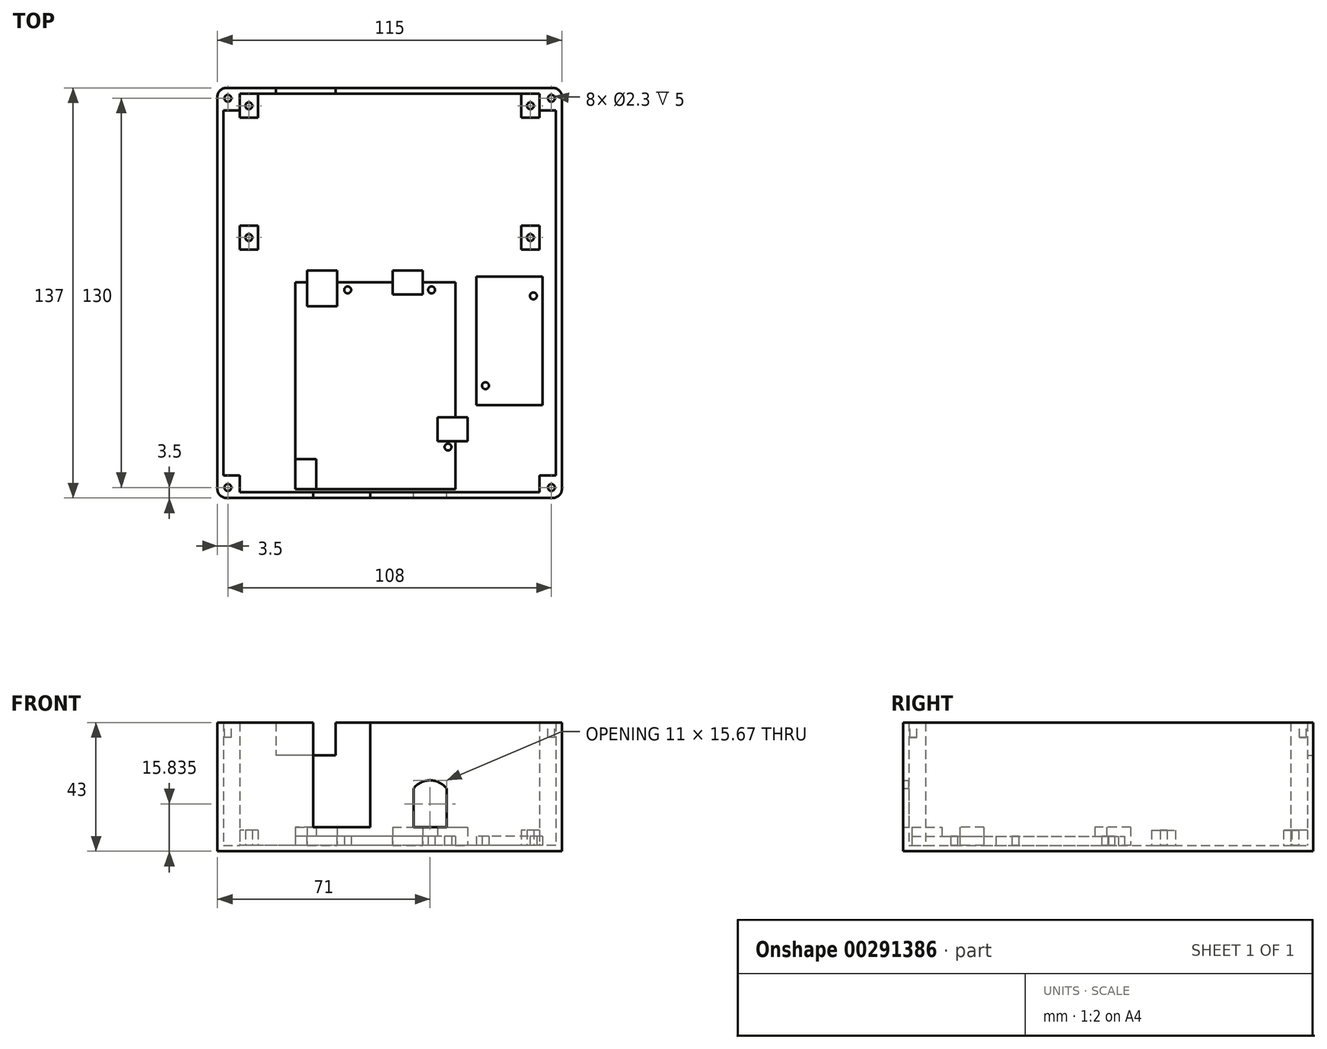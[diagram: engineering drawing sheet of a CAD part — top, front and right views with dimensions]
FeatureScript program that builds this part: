
annotation { "Feature Type Name" : "Feature", "Feature Type Description" : "" }
export const myFeature = defineFeature(function(context is Context, id is Id, definition is map)
    precondition{}
    {
        {
            var Q0;
            Q0=qCreatedBy(makeId("Top.planeOp"),FACE);
            var sketch = newSketch(context, id + "F0", { "sketchPlane" : qUnion([Q0])});
            skLineSegment(sketch, "E0.bottom", {"start": v(57.5, -68.5) * mm, "end": v(-57.5, -68.5) * mm});
            skLineSegment(sketch, "E0.top", {"start": v(57.5, 68.5) * mm, "end": v(-57.5, 68.5) * mm});
            skLineSegment(sketch, "E0.left", {"start": v(57.5, -68.5) * mm, "end": v(57.5, 68.5) * mm});
            skLineSegment(sketch, "E0.right", {"start": v(-57.5, -68.5) * mm, "end": v(-57.5, 68.5) * mm});
            skPoint(sketch, "E0.middle", {"position": v(0, 0) * mm});
            skSolve(sketch);
        }
        {
            var Q0;
            Q0 = qSketchRegion(id + "F0", true);
            extrude(context, id + "F1", {"entities" : qUnion([Q0]), "depth" : 2 * mm});
        }
        {
            var Q0;
            Q0=makeQuery(id+"F1.opExtrude","CAP_FACE",FACE,{"disambiguationData":[OSD([sQuery(id+"F0.wireOp",EDGE,"E0.bottom"),sQuery(id+"F0.wireOp",EDGE,"E0.top"),sQuery(id+"F0.wireOp",EDGE,"E0.left"),sQuery(id+"F0.wireOp",EDGE,"E0.right")])],"isStart":false});
            var sketch = newSketch(context, id + "F2", { "sketchPlane" : qUnion([Q0])});
            skLineSegment(sketch, "E1.bottom", {"start": v(57.5, -68.5) * mm, "end": v(-57.5, -68.5) * mm});
            skLineSegment(sketch, "E1.top", {"start": v(57.5, 68.5) * mm, "end": v(-57.5, 68.5) * mm});
            skLineSegment(sketch, "E1.left", {"start": v(57.5, -68.5) * mm, "end": v(57.5, 68.5) * mm});
            skLineSegment(sketch, "E1.right", {"start": v(-57.5, -68.5) * mm, "end": v(-57.5, 68.5) * mm});
            skPoint(sketch, "E1.middle", {"position": v(0, 0) * mm});
            skLineSegment(sketch, "E2.bottom", {"start": v(55.5, -66.5) * mm, "end": v(-55.5, -66.5) * mm});
            skLineSegment(sketch, "E2.top", {"start": v(55.5, 66.5) * mm, "end": v(-55.5, 66.5) * mm});
            skLineSegment(sketch, "E2.left", {"start": v(55.5, -66.5) * mm, "end": v(55.5, 66.5) * mm});
            skLineSegment(sketch, "E2.right", {"start": v(-55.5, -66.5) * mm, "end": v(-55.5, 66.5) * mm});
            skSolve(sketch);
        }
        {
            var Q0;
            Q0 = qSketchRegion(id + "F2", true);
            extrude(context, id + "F3", {"entities" : qUnion([Q0]), "operationType" : NewBodyOperationType.ADD, "depth" : 41 * mm});
        }
        {
            var Q0;
            Q0=makeQuery(id+"F1.opExtrude","CAP_FACE",FACE,{"disambiguationData":[OSD([sQuery(id+"F0.wireOp",EDGE,"E0.bottom"),sQuery(id+"F0.wireOp",EDGE,"E0.top"),sQuery(id+"F0.wireOp",EDGE,"E0.left"),sQuery(id+"F0.wireOp",EDGE,"E0.right")])],"isStart":false});
            var sketch = newSketch(context, id + "F4", { "sketchPlane" : qUnion([Q0])});
            skLineSegment(sketch, "E3.bottom", {"start": v(50, 15.5) * mm, "end": v(-50, 15.5) * mm, "construction": true});
            skLineSegment(sketch, "E3.top", {"start": v(50, 65.5) * mm, "end": v(-50, 65.5) * mm, "construction": true});
            skLineSegment(sketch, "E3.left", {"start": v(50, 15.5) * mm, "end": v(50, 65.5) * mm, "construction": true});
            skLineSegment(sketch, "E3.right", {"start": v(-50, 15.5) * mm, "end": v(-50, 65.5) * mm, "construction": true});
            skPoint(sketch, "E3.middle", {"position": v(0, 40.5) * mm});
            skCircle(sketch, "E4", {"center": v(-47, 62.5) * mm, "radius": 1.15 * mm});
            skCircle(sketch, "E5", {"center": v(47, 62.5) * mm, "radius": 1.15 * mm});
            skCircle(sketch, "E6", {"center": v(-47, 18.5) * mm, "radius": 1.15 * mm});
            skCircle(sketch, "E7", {"center": v(47, 18.5) * mm, "radius": 1.15 * mm});
            skLineSegment(sketch, "E8.bottom", {"start": v(-44, 66.5) * mm, "end": v(-50, 66.5) * mm});
            skLineSegment(sketch, "E8.top", {"start": v(-44, 58.5) * mm, "end": v(-50, 58.5) * mm});
            skLineSegment(sketch, "E8.left", {"start": v(-44, 66.5) * mm, "end": v(-44, 58.5) * mm});
            skLineSegment(sketch, "E8.right", {"start": v(-50, 66.5) * mm, "end": v(-50, 58.5) * mm});
            skLineSegment(sketch, "E9.bottom", {"start": v(50, 58.5) * mm, "end": v(44, 58.5) * mm});
            skLineSegment(sketch, "E9.top", {"start": v(50, 66.5) * mm, "end": v(44, 66.5) * mm});
            skLineSegment(sketch, "E9.left", {"start": v(50, 58.5) * mm, "end": v(50, 66.5) * mm});
            skLineSegment(sketch, "E9.right", {"start": v(44, 58.5) * mm, "end": v(44, 66.5) * mm});
            skLineSegment(sketch, "E10.bottom", {"start": v(-44, 14.5) * mm, "end": v(-50, 14.5) * mm});
            skLineSegment(sketch, "E10.top", {"start": v(-44, 22.5) * mm, "end": v(-50, 22.5) * mm});
            skLineSegment(sketch, "E10.left", {"start": v(-44, 14.5) * mm, "end": v(-44, 22.5) * mm});
            skLineSegment(sketch, "E10.right", {"start": v(-50, 14.5) * mm, "end": v(-50, 22.5) * mm});
            skLineSegment(sketch, "E11.bottom", {"start": v(50, 14.5) * mm, "end": v(44, 14.5) * mm});
            skLineSegment(sketch, "E11.top", {"start": v(50, 22.5) * mm, "end": v(44, 22.5) * mm});
            skLineSegment(sketch, "E11.left", {"start": v(50, 14.5) * mm, "end": v(50, 22.5) * mm});
            skLineSegment(sketch, "E11.right", {"start": v(44, 14.5) * mm, "end": v(44, 22.5) * mm});
            skSolve(sketch);
        }
        {
            var Q0;
            Q0 = qSketchRegion(id + "F4", true);
            extrude(context, id + "F5", {"entities" : qUnion([Q0]), "operationType" : NewBodyOperationType.ADD, "depth" : 5 * mm});
        }
        {
            var Q0;
            Q0=makeQuery(id+"F5.boolean.opBoolean","SPLIT",FACE,{"disambiguationData":[TD([makeQuery(id+"F3.opExtrude","SWEPT_FACE",FACE,{"disambiguationData":[OSD([sQuery(id+"F2.wireOp",EDGE,"E2.bottom")])]})])],"derivedFrom":makeQuery(id+"F1.opExtrude","CAP_FACE",FACE,{"disambiguationData":[OSD([sQuery(id+"F0.wireOp",EDGE,"E0.bottom"),sQuery(id+"F0.wireOp",EDGE,"E0.top"),sQuery(id+"F0.wireOp",EDGE,"E0.left"),sQuery(id+"F0.wireOp",EDGE,"E0.right")])],"isStart":false})});
            var sketch = newSketch(context, id + "F6", { "sketchPlane" : qUnion([Q0])});
            skLineSegment(sketch, "E12.bottom", {"start": v(51, -37.5) * mm, "end": v(29, -37.5) * mm});
            skLineSegment(sketch, "E12.top", {"start": v(51, 5.5) * mm, "end": v(29, 5.5) * mm});
            skLineSegment(sketch, "E12.left", {"start": v(51, -37.5) * mm, "end": v(51, 5.5) * mm});
            skLineSegment(sketch, "E12.right", {"start": v(29, -37.5) * mm, "end": v(29, 5.5) * mm});
            skPoint(sketch, "E12.middle", {"position": v(40, -16) * mm});
            skCircle(sketch, "E13", {"center": v(48, -1) * mm, "radius": 1.15 * mm});
            skCircle(sketch, "E14", {"center": v(32, -31) * mm, "radius": 1.15 * mm});
            skSolve(sketch);
        }
        {
            var Q0;
            Q0 = qSketchRegion(id + "F6", true);
            extrude(context, id + "F7", {"entities" : qUnion([Q0]), "operationType" : NewBodyOperationType.ADD, "depth" : 3 * mm});
        }
        {
            var Q0;
            Q0=makeQuery(id+"F5.boolean.opBoolean","SPLIT",FACE,{"disambiguationData":[TD([makeQuery(id+"F3.opExtrude","SWEPT_FACE",FACE,{"disambiguationData":[OSD([sQuery(id+"F2.wireOp",EDGE,"E2.bottom")])]})])],"derivedFrom":makeQuery(id+"F1.opExtrude","CAP_FACE",FACE,{"disambiguationData":[OSD([sQuery(id+"F0.wireOp",EDGE,"E0.bottom"),sQuery(id+"F0.wireOp",EDGE,"E0.top"),sQuery(id+"F0.wireOp",EDGE,"E0.left"),sQuery(id+"F0.wireOp",EDGE,"E0.right")])],"isStart":false})});
            var sketch = newSketch(context, id + "F8", { "sketchPlane" : qUnion([Q0])});
            skLineSegment(sketch, "E15.bottom", {"start": v(22, -65.5) * mm, "end": v(-31.5, -65.5) * mm});
            skLineSegment(sketch, "E15.top", {"start": v(22, 3.5) * mm, "end": v(-31.5, 3.5) * mm});
            skLineSegment(sketch, "E15.left", {"start": v(22, -65.5) * mm, "end": v(22, 3.5) * mm});
            skLineSegment(sketch, "E15.right", {"start": v(-31.5, -65.5) * mm, "end": v(-31.5, 3.5) * mm});
            skPoint(sketch, "E15.middle", {"position": v(-4.75, -31) * mm});
            skCircle(sketch, "E16", {"center": v(19.5, -51.5) * mm, "radius": 1.15 * mm});
            skCircle(sketch, "E17", {"center": v(14, 1) * mm, "radius": 1.15 * mm});
            skCircle(sketch, "E18", {"center": v(-14, 1) * mm, "radius": 1.15 * mm});
            skSolve(sketch);
        }
        {
            var Q0;
            {var subQ0=sQuery(id+"F8.wireOp",EDGE,"E15.top");Q0=makeQuery(id+"F8.imprint","IMPRINT",FACE,{"disambiguationData":[TD([[makeQuery(id+"F8.imprint","IMPRINT",EDGE,{"derivedFrom":subQ0}),1.0]])]});}
            extrude(context, id + "F9", {"entities" : qUnion([Q0]), "operationType" : NewBodyOperationType.ADD, "depth" : 3 * mm});
        }
        {
            var Q0;
            {var subQ15=makeQuery(id+"F3.opExtrude","SWEPT_FACE",FACE,{"disambiguationData":[OSD([sQuery(id+"F2.wireOp",EDGE,"E2.bottom")])]});Q0=makeQuery(id+"F9.boolean.opBoolean","SPLIT",FACE,{"disambiguationData":[TD([subQ15])],"derivedFrom":makeQuery(id+"F7.boolean.opBoolean","SPLIT",FACE,{"disambiguationData":[TD([subQ15])],"derivedFrom":makeQuery(id+"F5.boolean.opBoolean","SPLIT",FACE,{"disambiguationData":[TD([subQ15])],"derivedFrom":makeQuery(id+"F1.opExtrude","CAP_FACE",FACE,{"disambiguationData":[OSD([sQuery(id+"F0.wireOp",EDGE,"E0.bottom"),sQuery(id+"F0.wireOp",EDGE,"E0.top"),sQuery(id+"F0.wireOp",EDGE,"E0.left"),sQuery(id+"F0.wireOp",EDGE,"E0.right")])],"isStart":false})})})});}
            var sketch = newSketch(context, id + "F10", { "sketchPlane" : qUnion([Q0])});
            skLineSegment(sketch, "E19.bottom", {"start": v(1, 7.5) * mm, "end": v(11, 7.5) * mm});
            skLineSegment(sketch, "E19.top", {"start": v(1, -0.5) * mm, "end": v(11, -0.5) * mm});
            skLineSegment(sketch, "E19.left", {"start": v(1, 7.5) * mm, "end": v(1, -0.5) * mm});
            skLineSegment(sketch, "E19.right", {"start": v(11, 7.5) * mm, "end": v(11, -0.5) * mm});
            skLineSegment(sketch, "E20.bottom", {"start": v(16, -41.5) * mm, "end": v(26, -41.5) * mm});
            skLineSegment(sketch, "E20.top", {"start": v(16, -49.5) * mm, "end": v(26, -49.5) * mm});
            skLineSegment(sketch, "E20.left", {"start": v(16, -41.5) * mm, "end": v(16, -49.5) * mm});
            skLineSegment(sketch, "E20.right", {"start": v(26, -41.5) * mm, "end": v(26, -49.5) * mm});
            skLineSegment(sketch, "E21.bottom", {"start": v(-31.5, -55.5) * mm, "end": v(-24.5, -55.5) * mm});
            skLineSegment(sketch, "E21.top", {"start": v(-31.5, -65.5) * mm, "end": v(-24.5, -65.5) * mm});
            skLineSegment(sketch, "E21.left", {"start": v(-31.5, -55.5) * mm, "end": v(-31.5, -65.5) * mm});
            skLineSegment(sketch, "E21.right", {"start": v(-24.5, -55.5) * mm, "end": v(-24.5, -65.5) * mm});
            skLineSegment(sketch, "E22.bottom", {"start": v(-27.5, 7.5) * mm, "end": v(-17.5, 7.5) * mm});
            skLineSegment(sketch, "E22.top", {"start": v(-27.5, -4.5) * mm, "end": v(-17.5, -4.5) * mm});
            skLineSegment(sketch, "E22.left", {"start": v(-27.5, 7.5) * mm, "end": v(-27.5, -4.5) * mm});
            skLineSegment(sketch, "E22.right", {"start": v(-17.5, 7.5) * mm, "end": v(-17.5, -4.5) * mm});
            skSolve(sketch);
        }
        {
            var Q0;
            Q0 = qSketchRegion(id + "F10", true);
            extrude(context, id + "F11", {"entities" : qUnion([Q0]), "operationType" : NewBodyOperationType.ADD, "depth" : 6 * mm});
        }
        {
            var Q0;
            Q0=makeQuery(id+"F3.opExtrude","SWEPT_FACE",FACE,{"disambiguationData":[OSD([sQuery(id+"F2.wireOp",EDGE,"E2.bottom")])]});
            var sketch = newSketch(context, id + "F12", { "sketchPlane" : qUnion([Q0])});
            skLineSegment(sketch, "E23.bottom", {"start": v(6.5, 40) * mm, "end": v(25.5, 40) * mm});
            skLineSegment(sketch, "E23.top", {"start": v(6.5, 8) * mm, "end": v(25.5, 8) * mm});
            skLineSegment(sketch, "E23.left", {"start": v(6.5, 40) * mm, "end": v(6.5, 8) * mm});
            skLineSegment(sketch, "E23.right", {"start": v(25.5, 40) * mm, "end": v(25.5, 8) * mm});
            skLineSegment(sketch, "E24.bottom", {"start": v(-8, 21) * mm, "end": v(-19, 21) * mm, "construction": true});
            skLineSegment(sketch, "E24.top", {"start": v(-8, 8) * mm, "end": v(-19, 8) * mm});
            skLineSegment(sketch, "E24.left", {"start": v(-8, 21) * mm, "end": v(-8, 8) * mm});
            skLineSegment(sketch, "E24.right", {"start": v(-19, 21) * mm, "end": v(-19, 8) * mm});
            skLineSegment(sketch, "E25.bottom", {"start": v(25.5, 40) * mm, "end": v(6.5, 40) * mm});
            skLineSegment(sketch, "E25.top", {"start": v(25.5, 45.22) * mm, "end": v(6.5, 45.22) * mm});
            skLineSegment(sketch, "E25.left", {"start": v(25.5, 40) * mm, "end": v(25.5, 45.22) * mm});
            skLineSegment(sketch, "E25.right", {"start": v(6.5, 40) * mm, "end": v(6.5, 45.22) * mm});
            skArc(sketch, "E26", {"start": v(-8, 21) * mm, "mid": v(-13.5, 23.67) * mm, "end": v(-19, 21) * mm});
            skSolve(sketch);
        }
        {
            var Q0;
            Q0 = qSketchRegion(id + "F12", true);
            extrude(context, id + "F13", {"entities" : qUnion([Q0]), "operationType" : NewBodyOperationType.REMOVE, "oppositeDirection" : true, "depth" : 2 * mm});
        }
        {
            var Q0;
            Q0=makeQuery(id+"F3.boolean.opBoolean","MERGE",FACE,{"derivedFrom":[makeQuery(id+"F1.opExtrude","SWEPT_FACE",FACE,{"disambiguationData":[OSD([sQuery(id+"F0.wireOp",EDGE,"E0.top")])]}),makeQuery(id+"F3.opExtrude","SWEPT_FACE",FACE,{"disambiguationData":[OSD([sQuery(id+"F2.wireOp",EDGE,"E1.top")])]})]});
            var sketch = newSketch(context, id + "F14", { "sketchPlane" : qUnion([Q0])});
            skLineSegment(sketch, "E27.bottom", {"start": v(18, 43) * mm, "end": v(38, 43) * mm});
            skLineSegment(sketch, "E27.top", {"start": v(18, 32) * mm, "end": v(38, 32) * mm});
            skLineSegment(sketch, "E27.left", {"start": v(18, 43) * mm, "end": v(18, 32) * mm});
            skLineSegment(sketch, "E27.right", {"start": v(38, 43) * mm, "end": v(38, 32) * mm});
            skSolve(sketch);
        }
        {
            var Q0;
            Q0 = qSketchRegion(id + "F14", true);
            extrude(context, id + "F15", {"entities" : qUnion([Q0]), "operationType" : NewBodyOperationType.REMOVE, "oppositeDirection" : true, "depth" : 2 * mm});
        }
        {
            var Q0;
            {var subQ15=makeQuery(id+"F3.opExtrude","SWEPT_FACE",FACE,{"disambiguationData":[OSD([sQuery(id+"F2.wireOp",EDGE,"E2.bottom")])]});Q0=makeQuery(id+"F9.boolean.opBoolean","SPLIT",FACE,{"disambiguationData":[TD([subQ15])],"derivedFrom":makeQuery(id+"F7.boolean.opBoolean","SPLIT",FACE,{"disambiguationData":[TD([subQ15])],"derivedFrom":makeQuery(id+"F5.boolean.opBoolean","SPLIT",FACE,{"disambiguationData":[TD([subQ15])],"derivedFrom":makeQuery(id+"F1.opExtrude","CAP_FACE",FACE,{"disambiguationData":[OSD([sQuery(id+"F0.wireOp",EDGE,"E0.bottom"),sQuery(id+"F0.wireOp",EDGE,"E0.top"),sQuery(id+"F0.wireOp",EDGE,"E0.left"),sQuery(id+"F0.wireOp",EDGE,"E0.right")])],"isStart":false})})})});}
            var sketch = newSketch(context, id + "F16", { "sketchPlane" : qUnion([Q0])});
            skLineSegment(sketch, "E28.bottom", {"start": v(-55.5, -66.5) * mm, "end": v(-50, -66.5) * mm});
            skLineSegment(sketch, "E28.top", {"start": v(-55.5, -61) * mm, "end": v(-50, -61) * mm});
            skLineSegment(sketch, "E28.left", {"start": v(-55.5, -66.5) * mm, "end": v(-55.5, -61) * mm});
            skLineSegment(sketch, "E28.right", {"start": v(-50, -66.5) * mm, "end": v(-50, -61) * mm});
            skLineSegment(sketch, "E29.bottom", {"start": v(-55.5, 66.5) * mm, "end": v(-50, 66.5) * mm});
            skLineSegment(sketch, "E29.top", {"start": v(-55.5, 61) * mm, "end": v(-50, 61) * mm});
            skLineSegment(sketch, "E29.left", {"start": v(-55.5, 66.5) * mm, "end": v(-55.5, 61) * mm});
            skLineSegment(sketch, "E29.right", {"start": v(-50, 66.5) * mm, "end": v(-50, 61) * mm});
            skLineSegment(sketch, "E30.bottom", {"start": v(55.5, 66.5) * mm, "end": v(50, 66.5) * mm});
            skLineSegment(sketch, "E30.top", {"start": v(55.5, 61) * mm, "end": v(50, 61) * mm});
            skLineSegment(sketch, "E30.left", {"start": v(55.5, 66.5) * mm, "end": v(55.5, 61) * mm});
            skLineSegment(sketch, "E30.right", {"start": v(50, 66.5) * mm, "end": v(50, 61) * mm});
            skLineSegment(sketch, "E31.bottom", {"start": v(55.5, -66.5) * mm, "end": v(50, -66.5) * mm});
            skLineSegment(sketch, "E31.top", {"start": v(55.5, -61) * mm, "end": v(50, -61) * mm});
            skLineSegment(sketch, "E31.left", {"start": v(55.5, -66.5) * mm, "end": v(55.5, -61) * mm});
            skLineSegment(sketch, "E31.right", {"start": v(50, -66.5) * mm, "end": v(50, -61) * mm});
            skSolve(sketch);
        }
        {
            var Q0;
            Q0 = qSketchRegion(id + "F16", true);
            extrude(context, id + "F17", {"entities" : qUnion([Q0]), "operationType" : NewBodyOperationType.ADD, "depth" : 41 * mm});
        }
        {
            var Q0;
            Q0=makeQuery(id+"F17.opExtrude","CAP_FACE",FACE,{"disambiguationData":[OSD([sQuery(id+"F16.wireOp",EDGE,"E28.bottom"),sQuery(id+"F16.wireOp",EDGE,"E28.top"),sQuery(id+"F16.wireOp",EDGE,"E28.left"),sQuery(id+"F16.wireOp",EDGE,"E28.right")])],"isStart":false});
            var sketch = newSketch(context, id + "F18", { "sketchPlane" : qUnion([Q0])});
            skCircle(sketch, "E32", {"center": v(-54, -65) * mm, "radius": 1.15 * mm});
            skCircle(sketch, "E33", {"center": v(-54, 65) * mm, "radius": 1.15 * mm});
            skCircle(sketch, "E34", {"center": v(54, 65) * mm, "radius": 1.15 * mm});
            skCircle(sketch, "E35", {"center": v(54, -65) * mm, "radius": 1.15 * mm});
            skSolve(sketch);
        }
        {
            var Q0;
            Q0 = qSketchRegion(id + "F18", true);
            extrude(context, id + "F19", {"entities" : qUnion([Q0]), "operationType" : NewBodyOperationType.REMOVE, "oppositeDirection" : true, "depth" : 5 * mm});
        }
        {
            var Q0;
            Q0=makeQuery(id+"F3.boolean.opBoolean","MERGE",EDGE,{"derivedFrom":[makeQuery(id+"F1.opExtrude","SWEPT_EDGE",EDGE,{"disambiguationData":[OSD([sQuery(id+"F0.wireOp",EDGE,"E0.bottom"),sQuery(id+"F0.wireOp",EDGE,"E0.right")])]}),makeQuery(id+"F3.opExtrude","SWEPT_EDGE",EDGE,{"disambiguationData":[OSD([sQuery(id+"F2.wireOp",EDGE,"E1.bottom"),sQuery(id+"F2.wireOp",EDGE,"E1.right")])]})]});
            var Q1;
            Q1=makeQuery(id+"F3.boolean.opBoolean","MERGE",EDGE,{"derivedFrom":[makeQuery(id+"F1.opExtrude","SWEPT_EDGE",EDGE,{"disambiguationData":[OSD([sQuery(id+"F0.wireOp",EDGE,"E0.bottom"),sQuery(id+"F0.wireOp",EDGE,"E0.left")])]}),makeQuery(id+"F3.opExtrude","SWEPT_EDGE",EDGE,{"disambiguationData":[OSD([sQuery(id+"F2.wireOp",EDGE,"E1.bottom"),sQuery(id+"F2.wireOp",EDGE,"E1.left")])]})]});
            var Q2;
            Q2=makeQuery(id+"F3.boolean.opBoolean","MERGE",EDGE,{"derivedFrom":[makeQuery(id+"F1.opExtrude","SWEPT_EDGE",EDGE,{"disambiguationData":[OSD([sQuery(id+"F0.wireOp",EDGE,"E0.top"),sQuery(id+"F0.wireOp",EDGE,"E0.left")])]}),makeQuery(id+"F3.opExtrude","SWEPT_EDGE",EDGE,{"disambiguationData":[OSD([sQuery(id+"F2.wireOp",EDGE,"E1.top"),sQuery(id+"F2.wireOp",EDGE,"E1.left")])]})]});
            var Q3;
            Q3=makeQuery(id+"F3.boolean.opBoolean","MERGE",EDGE,{"derivedFrom":[makeQuery(id+"F1.opExtrude","SWEPT_EDGE",EDGE,{"disambiguationData":[OSD([sQuery(id+"F0.wireOp",EDGE,"E0.top"),sQuery(id+"F0.wireOp",EDGE,"E0.right")])]}),makeQuery(id+"F3.opExtrude","SWEPT_EDGE",EDGE,{"disambiguationData":[OSD([sQuery(id+"F2.wireOp",EDGE,"E1.top"),sQuery(id+"F2.wireOp",EDGE,"E1.right")])]})]});
            fillet(context, id + "F20", {"entities" : qUnion([Q0, Q1, Q2, Q3]), "radius" : 3 * mm, "tangentPropagation" : true, "allowEdgeOverflow" : false});
        }
    });
